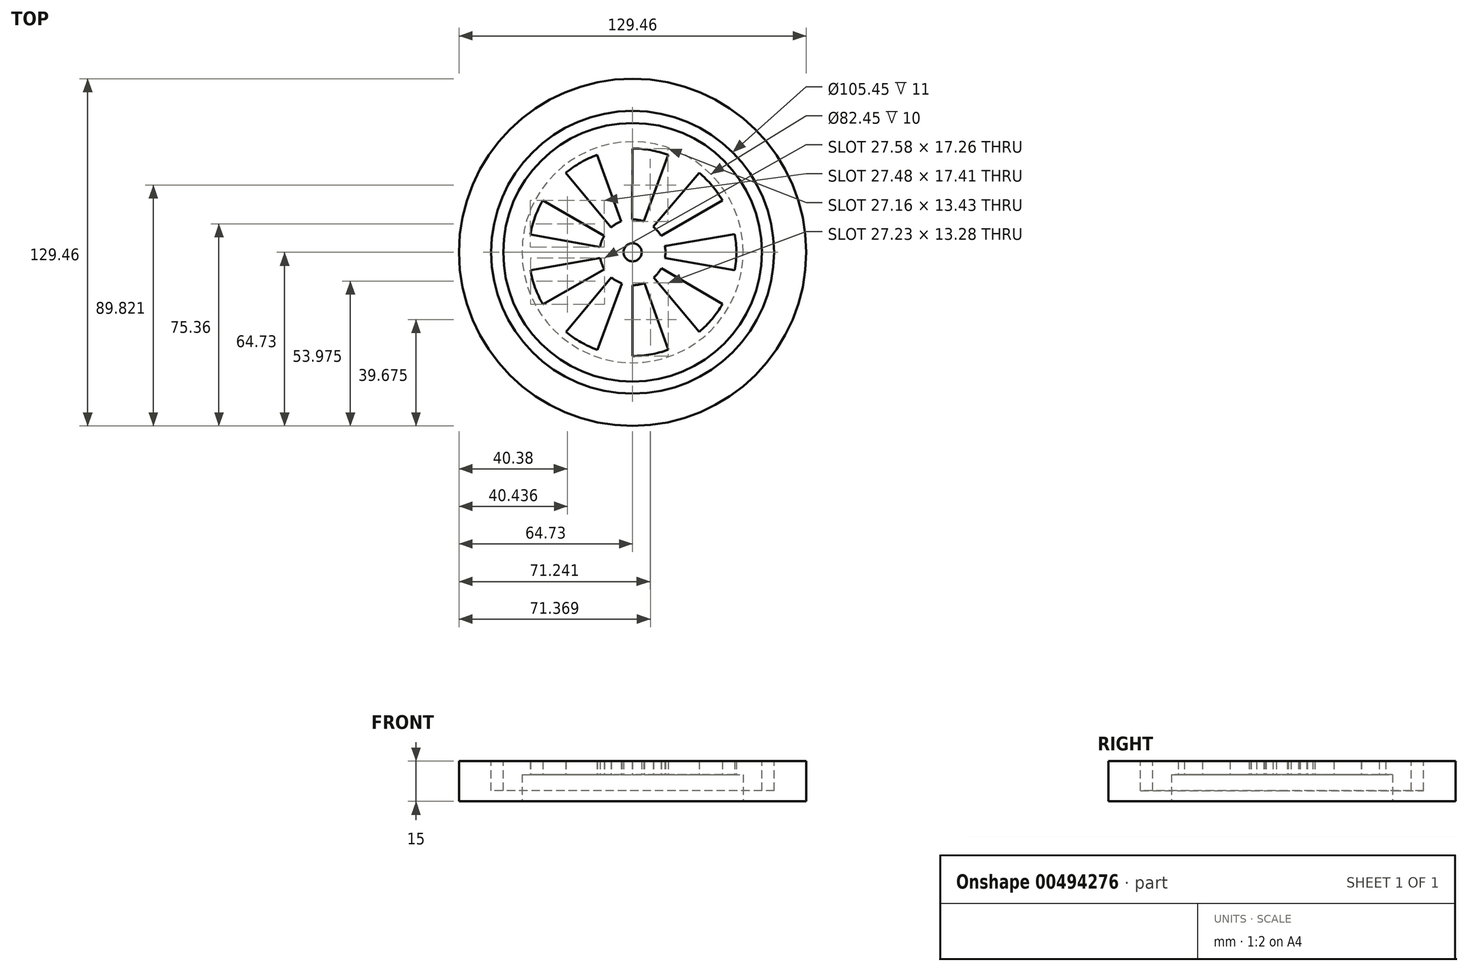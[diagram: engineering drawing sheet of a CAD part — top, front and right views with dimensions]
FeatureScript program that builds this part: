
annotation { "Feature Type Name" : "Feature", "Feature Type Description" : "" }
export const myFeature = defineFeature(function(context is Context, id is Id, definition is map)
    precondition{}
    {
        {
            var Q0;
            Q0=qCreatedBy(makeId("Top.planeOp"),FACE);
            var sketch = newSketch(context, id + "F0", { "sketchPlane" : qUnion([Q0])});
            skCircle(sketch, "E0", {"center": v(0, 0) * mm, "radius": 64.73 * mm});
            skSolve(sketch);
        }
        {
            var Q0;
            Q0=qSketchRegion(id+"F0",true);
            extrude(context, id + "F1", {"entities" : qUnion([Q0]), "depth" : 15 * mm});
        }
        {
            var Q0;
            Q0=makeQuery(id+"F1.opExtrude","CAP_FACE",FACE,{"disambiguationData":[OSD([sQuery(id+"F0.wireOp",EDGE,"E0")])],"isStart":false});
            var sketch = newSketch(context, id + "F2", { "sketchPlane" : qUnion([Q0])});
            skCircle(sketch, "E1", {"center": v(0, 0) * mm, "radius": 52.73 * mm});
            skCircle(sketch, "E2", {"center": v(0, 0) * mm, "radius": 48.23 * mm});
            skSolve(sketch);
        }
        {
            var Q0;
            Q0=makeQuery(id+"F2.imprint","IMPRINT",FACE,{"disambiguationData":[TD([[makeQuery(id+"F2.imprint","IMPRINT",EDGE,{"derivedFrom":sQuery(id+"F2.wireOp",EDGE,"E1")}),1.0]])]});
            extrude(context, id + "F3", {"entities" : qUnion([Q0]), "operationType" : NewBodyOperationType.REMOVE, "oppositeDirection" : true, "depth" : 11 * mm});
        }
        {
            var Q0;
            Q0=makeQuery(id+"F1.opExtrude","CAP_FACE",FACE,{"disambiguationData":[OSD([sQuery(id+"F0.wireOp",EDGE,"E0")])],"isStart":true});
            var sketch = newSketch(context, id + "F4", { "sketchPlane" : qUnion([Q0])});
            skCircle(sketch, "E3", {"center": v(0, 0) * mm, "radius": 41.23 * mm});
            skSolve(sketch);
        }
        {
            var Q0;
            Q0=makeQuery(id+"F4.imprint","IMPRINT",FACE,{"disambiguationData":[TD([[makeQuery(id+"F4.imprint","IMPRINT",EDGE,{"derivedFrom":sQuery(id+"F4.wireOp",EDGE,"E3")}),1.0]])]});
            extrude(context, id + "F5", {"entities" : qUnion([Q0]), "operationType" : NewBodyOperationType.REMOVE, "oppositeDirection" : true, "depth" : 10 * mm});
        }
        {
            var Q0;
            Q0=makeQuery(id+"F5.boolean.opBoolean","COPY",FACE,{"derivedFrom":makeQuery(id+"F5.opExtrude","CAP_FACE",FACE,{"disambiguationData":[OSD([sQuery(id+"F4.wireOp",EDGE,"E3")])],"isStart":false})});
            var sketch = newSketch(context, id + "F6", { "sketchPlane" : qUnion([Q0])});
            skArc(sketch, "E4.0", {"start": v(4.38, 11.44) * mm, "mid": v(2.23, 12.05) * mm, "end": v(0, 12.25) * mm});
            skArc(sketch, "E5.0", {"start": v(13.28, 36.32) * mm, "mid": v(6.74, 38.08) * mm, "end": v(0, 38.67) * mm});
            skLineSegment(sketch, "E6", {"start": v(0, 38.67) * mm, "end": v(0, 12.25) * mm});
            skLineSegment(sketch, "E7", {"start": v(4.38, 11.44) * mm, "end": v(13.28, 36.32) * mm});
            skArc(sketch, "E8.1.0", {"start": v(-13.17, 36.36) * mm, "mid": v(-19.31, 33.5) * mm, "end": v(-24.86, 29.62) * mm});
            skLineSegment(sketch, "E8.1.1", {"start": v(-4, 11.58) * mm, "end": v(-13.17, 36.36) * mm});
            skArc(sketch, "E8.1.2", {"start": v(-4, 11.58) * mm, "mid": v(-6.04, 10.66) * mm, "end": v(-7.87, 9.38) * mm});
            skLineSegment(sketch, "E8.1.3", {"start": v(-24.86, 29.62) * mm, "end": v(-7.87, 9.38) * mm});
            skArc(sketch, "E8.2.0", {"start": v(-33.46, 19.38) * mm, "mid": v(-36.33, 13.25) * mm, "end": v(-38.08, 6.71) * mm});
            skLineSegment(sketch, "E8.2.1", {"start": v(-10.5, 6.3) * mm, "end": v(-33.46, 19.38) * mm});
            skArc(sketch, "E8.2.2", {"start": v(-10.5, 6.3) * mm, "mid": v(-11.48, 4.29) * mm, "end": v(-12.06, 2.13) * mm});
            skLineSegment(sketch, "E8.2.3", {"start": v(-38.08, 6.71) * mm, "end": v(-12.06, 2.13) * mm});
            skArc(sketch, "E8.3.0", {"start": v(-38.1, -6.66) * mm, "mid": v(-36.35, -13.2) * mm, "end": v(-33.49, -19.33) * mm});
            skLineSegment(sketch, "E8.3.1", {"start": v(-12.1, -1.93) * mm, "end": v(-38.1, -6.66) * mm});
            skArc(sketch, "E8.3.2", {"start": v(-12.1, -1.93) * mm, "mid": v(-11.55, -4.1) * mm, "end": v(-10.6, -6.13) * mm});
            skLineSegment(sketch, "E8.3.3", {"start": v(-33.49, -19.33) * mm, "end": v(-10.6, -6.13) * mm});
            skArc(sketch, "E8.4.0", {"start": v(-24.9, -29.59) * mm, "mid": v(-19.36, -33.48) * mm, "end": v(-13.23, -36.34) * mm});
            skLineSegment(sketch, "E8.4.1", {"start": v(-8.03, -9.25) * mm, "end": v(-24.9, -29.59) * mm});
            skArc(sketch, "E8.4.2", {"start": v(-8.03, -9.25) * mm, "mid": v(-6.21, -10.56) * mm, "end": v(-4.19, -11.51) * mm});
            skLineSegment(sketch, "E8.4.3", {"start": v(-13.23, -36.34) * mm, "end": v(-4.19, -11.51) * mm});
            skArc(sketch, "E8.5.0", {"start": v(-0.06, -38.67) * mm, "mid": v(6.69, -38.09) * mm, "end": v(13.23, -36.34) * mm});
            skLineSegment(sketch, "E8.5.1", {"start": v(-0.2, -12.25) * mm, "end": v(-0.06, -38.67) * mm});
            skArc(sketch, "E8.5.2", {"start": v(-0.2, -12.25) * mm, "mid": v(2.03, -12.08) * mm, "end": v(4.19, -11.51) * mm});
            skLineSegment(sketch, "E8.5.3", {"start": v(13.23, -36.34) * mm, "end": v(4.19, -11.51) * mm});
            skArc(sketch, "E8.6.0", {"start": v(24.81, -29.66) * mm, "mid": v(29.6, -24.88) * mm, "end": v(33.49, -19.33) * mm});
            skLineSegment(sketch, "E8.6.1", {"start": v(7.72, -9.51) * mm, "end": v(24.81, -29.66) * mm});
            skArc(sketch, "E8.6.2", {"start": v(7.72, -9.51) * mm, "mid": v(9.32, -7.95) * mm, "end": v(10.6, -6.13) * mm});
            skLineSegment(sketch, "E8.6.3", {"start": v(33.49, -19.33) * mm, "end": v(10.6, -6.13) * mm});
            skArc(sketch, "E8.7.0", {"start": v(38.07, -6.77) * mm, "mid": v(38.67, -0.03) * mm, "end": v(38.08, 6.71) * mm});
            skLineSegment(sketch, "E8.7.1", {"start": v(12.03, -2.33) * mm, "end": v(38.07, -6.77) * mm});
            skArc(sketch, "E8.7.2", {"start": v(12.03, -2.33) * mm, "mid": v(12.25, -0.1) * mm, "end": v(12.06, 2.13) * mm});
            skLineSegment(sketch, "E8.7.3", {"start": v(38.08, 6.71) * mm, "end": v(12.06, 2.13) * mm});
            skArc(sketch, "E8.8.0", {"start": v(33.52, 19.29) * mm, "mid": v(29.64, 24.84) * mm, "end": v(24.86, 29.62) * mm});
            skLineSegment(sketch, "E8.8.1", {"start": v(10.7, 5.95) * mm, "end": v(33.52, 19.29) * mm});
            skArc(sketch, "E8.8.2", {"start": v(10.7, 5.95) * mm, "mid": v(9.45, 7.8) * mm, "end": v(7.87, 9.38) * mm});
            skLineSegment(sketch, "E8.8.3", {"start": v(24.86, 29.62) * mm, "end": v(7.87, 9.38) * mm});
            skSolve(sketch);
        }
        {
            var Q0;
            Q0=makeQuery(id+"F6.imprint","IMPRINT",FACE,{"disambiguationData":[TD([[makeQuery(id+"F6.imprint","IMPRINT",EDGE,{"derivedFrom":sQuery(id+"F6.wireOp",EDGE,"E4.0")}),-1.0]])]});
            var Q1;
            Q1=makeQuery(id+"F6.imprint","IMPRINT",FACE,{"disambiguationData":[TD([[makeQuery(id+"F6.imprint","IMPRINT",EDGE,{"derivedFrom":sQuery(id+"F6.wireOp",EDGE,"E8.8.0")}),1.0]])]});
            var Q2;
            Q2=makeQuery(id+"F6.imprint","IMPRINT",FACE,{"disambiguationData":[TD([[makeQuery(id+"F6.imprint","IMPRINT",EDGE,{"derivedFrom":sQuery(id+"F6.wireOp",EDGE,"E8.7.0")}),1.0]])]});
            var Q3;
            Q3=makeQuery(id+"F6.imprint","IMPRINT",FACE,{"disambiguationData":[TD([[makeQuery(id+"F6.imprint","IMPRINT",EDGE,{"derivedFrom":sQuery(id+"F6.wireOp",EDGE,"E8.6.0")}),1.0]])]});
            var Q4;
            Q4=makeQuery(id+"F6.imprint","IMPRINT",FACE,{"disambiguationData":[TD([[makeQuery(id+"F6.imprint","IMPRINT",EDGE,{"derivedFrom":sQuery(id+"F6.wireOp",EDGE,"E8.5.0")}),1.0]])]});
            var Q5;
            Q5=makeQuery(id+"F6.imprint","IMPRINT",FACE,{"disambiguationData":[TD([[makeQuery(id+"F6.imprint","IMPRINT",EDGE,{"derivedFrom":sQuery(id+"F6.wireOp",EDGE,"E8.4.0")}),1.0]])]});
            var Q6;
            Q6=makeQuery(id+"F6.imprint","IMPRINT",FACE,{"disambiguationData":[TD([[makeQuery(id+"F6.imprint","IMPRINT",EDGE,{"derivedFrom":sQuery(id+"F6.wireOp",EDGE,"E8.3.0")}),1.0]])]});
            var Q7;
            Q7=makeQuery(id+"F6.imprint","IMPRINT",FACE,{"disambiguationData":[TD([[makeQuery(id+"F6.imprint","IMPRINT",EDGE,{"derivedFrom":sQuery(id+"F6.wireOp",EDGE,"E8.2.0")}),1.0]])]});
            var Q8;
            Q8=makeQuery(id+"F6.imprint","IMPRINT",FACE,{"disambiguationData":[TD([[makeQuery(id+"F6.imprint","IMPRINT",EDGE,{"derivedFrom":sQuery(id+"F6.wireOp",EDGE,"E8.1.0")}),1.0]])]});
            extrude(context, id + "F7", {"entities" : qUnion([Q0, Q1, Q2, Q3, Q4, Q5, Q6, Q7, Q8]), "operationType" : NewBodyOperationType.REMOVE, "endBound" : BoundingType.UP_TO_NEXT, "oppositeDirection" : true, "depth" : 25.4 * mm});
        }
        {
            var Q0;
            Q0=sQuery(id+"F6.wireOp",VERTEX,"E4.0.center");
            var Q1;
            Q1=makeQuery(id+"F1.opExtrude","SWEPT_BODY",BODY,{"disambiguationData":[OSD([sQuery(id+"F0.wireOp",EDGE,"E0")])]});
            hole(context, id + "F8", {"style" : HoleStyle.SIMPLE, "endStyle" : HoleEndStyle.THROUGH, "standardTappedOrClearance" : lookupTablePath({ "standard" : "ANSI", "fit" : "Normal (ASME)", "size" : "1/4", "type" : "Clearance" }), "standardBlindInLast" : lookupTablePath({ "fit" : "Free", "standard" : "ANSI", "size" : "1/4", "type" : "Clearance" }), "holeDiameter" : 6.76 * mm, "isTappedThrough" : true, "tappedDepth" : 12.7 * mm, "tapClearance" : 3, "locations" : qUnion([Q0]), "scope" : qUnion([Q1])});
        }
    });
